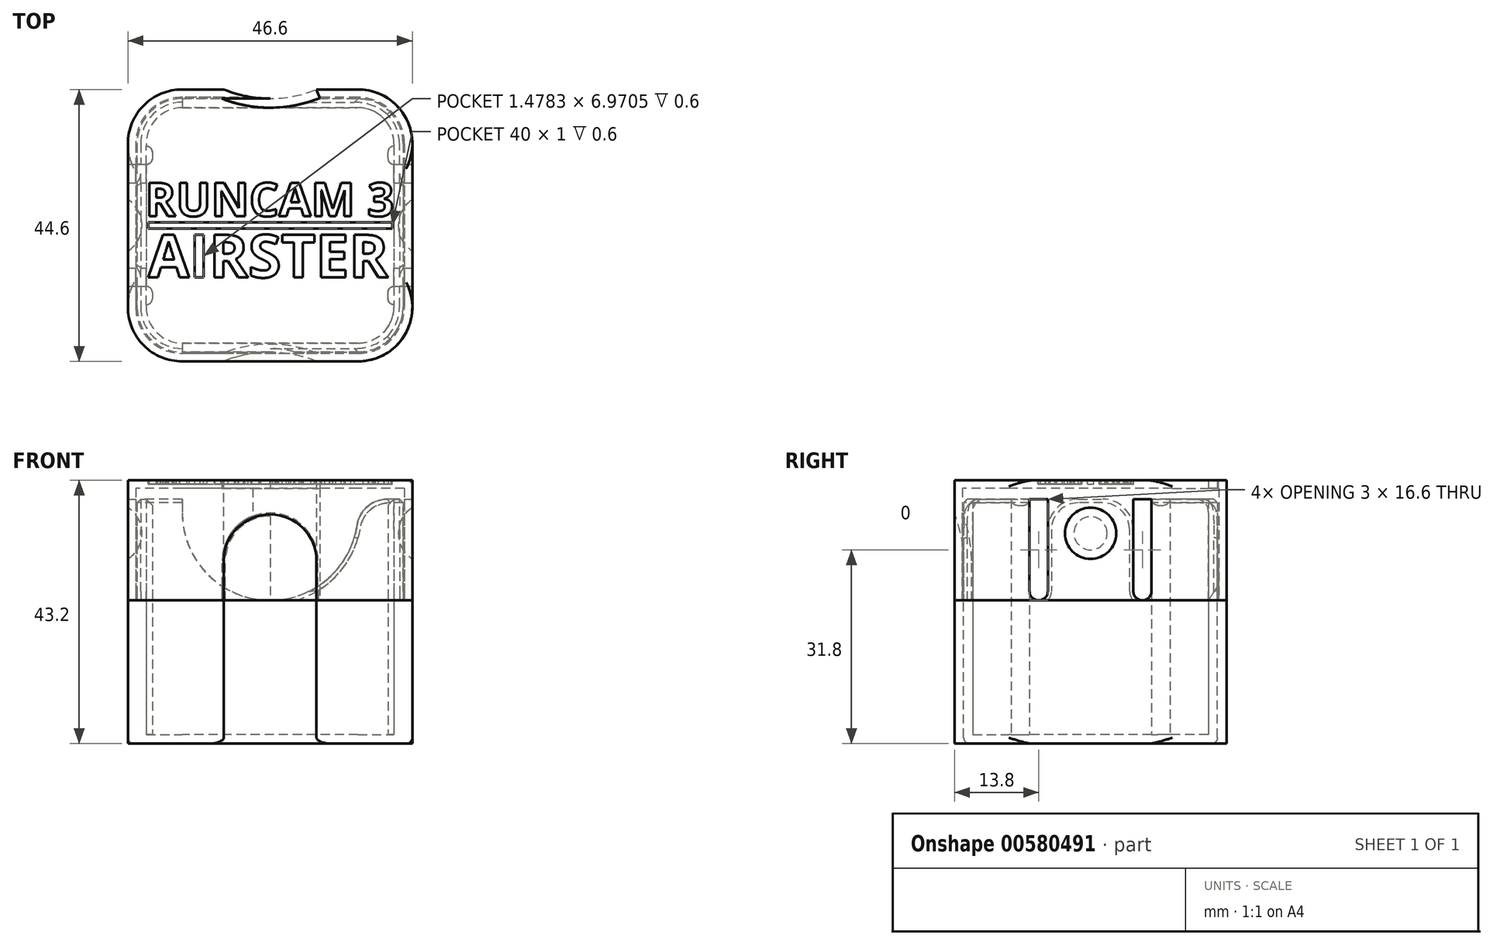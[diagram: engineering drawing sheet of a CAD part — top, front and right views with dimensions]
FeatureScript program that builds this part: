
annotation { "Feature Type Name" : "Feature", "Feature Type Description" : "" }
export const myFeature = defineFeature(function(context is Context, id is Id, definition is map)
    precondition{}
    {
        {
            var Q0;
            Q0=qCreatedBy(makeId("Top.planeOp"),FACE);
            var sketch = newSketch(context, id + "F0", { "sketchPlane" : qUnion([Q0])});
            skLineSegment(sketch, "E0.bottom", {"start": v(14.4, 19.3) * mm, "end": v(-14.4, 19.3) * mm});
            skLineSegment(sketch, "E0.top", {"start": v(14.4, -19.3) * mm, "end": v(-14.4, -19.3) * mm});
            skLineSegment(sketch, "E0.left", {"start": v(20.3, 13.4) * mm, "end": v(20.3, -13.4) * mm});
            skLineSegment(sketch, "E0.right", {"start": v(-20.3, 13.4) * mm, "end": v(-20.3, -13.4) * mm});
            skPoint(sketch, "E0.middle", {"position": v(0, 0) * mm});
            skPoint(sketch, "E1.visualSharp", {"position": v(-20.3, 19.3) * mm});
            skArc(sketch, "E1.filletArc", {"start": v(-14.4, 19.3) * mm, "mid": v(-18.57, 17.57) * mm, "end": v(-20.3, 13.4) * mm});
            skPoint(sketch, "E2.visualSharp", {"position": v(-20.3, -19.3) * mm});
            skArc(sketch, "E2.filletArc", {"start": v(-20.3, -13.4) * mm, "mid": v(-18.57, -17.57) * mm, "end": v(-14.4, -19.3) * mm});
            skPoint(sketch, "E3.visualSharp", {"position": v(20.3, -19.3) * mm});
            skArc(sketch, "E3.filletArc", {"start": v(14.4, -19.3) * mm, "mid": v(18.57, -17.57) * mm, "end": v(20.3, -13.4) * mm});
            skPoint(sketch, "E4.visualSharp", {"position": v(20.3, 19.3) * mm});
            skArc(sketch, "E4.filletArc", {"start": v(20.3, 13.4) * mm, "mid": v(18.57, 17.57) * mm, "end": v(14.4, 19.3) * mm});
            skArc(sketch, "E5.0", {"start": v(21.8, 13.4) * mm, "mid": v(19.63, 18.63) * mm, "end": v(14.4, 20.8) * mm});
            skLineSegment(sketch, "E5.1", {"start": v(14.4, 20.8) * mm, "end": v(-14.4, 20.8) * mm});
            skLineSegment(sketch, "E5.2", {"start": v(21.8, 13.4) * mm, "end": v(21.8, -13.4) * mm});
            skArc(sketch, "E5.3", {"start": v(-14.4, 20.8) * mm, "mid": v(-19.63, 18.63) * mm, "end": v(-21.8, 13.4) * mm});
            skArc(sketch, "E5.4", {"start": v(14.4, -20.8) * mm, "mid": v(19.63, -18.63) * mm, "end": v(21.8, -13.4) * mm});
            skLineSegment(sketch, "E5.5", {"start": v(14.4, -20.8) * mm, "end": v(-14.4, -20.8) * mm});
            skArc(sketch, "E5.6", {"start": v(-21.8, -13.4) * mm, "mid": v(-19.63, -18.63) * mm, "end": v(-14.4, -20.8) * mm});
            skLineSegment(sketch, "E5.7", {"start": v(-21.8, 13.4) * mm, "end": v(-21.8, -13.4) * mm});
            skLineSegment(sketch, "E6.0", {"start": v(23.3, 13.4) * mm, "end": v(23.3, -13.4) * mm});
            skArc(sketch, "E6.1", {"start": v(14.4, -22.3) * mm, "mid": v(20.7, -19.7) * mm, "end": v(23.3, -13.4) * mm});
            skArc(sketch, "E6.2", {"start": v(23.3, 13.4) * mm, "mid": v(20.7, 19.7) * mm, "end": v(14.4, 22.3) * mm});
            skLineSegment(sketch, "E6.3", {"start": v(14.4, -22.3) * mm, "end": v(-14.4, -22.3) * mm});
            skLineSegment(sketch, "E6.4", {"start": v(14.4, 22.3) * mm, "end": v(-14.4, 22.3) * mm});
            skArc(sketch, "E6.5", {"start": v(-14.4, 22.3) * mm, "mid": v(-20.7, 19.7) * mm, "end": v(-23.3, 13.4) * mm});
            skLineSegment(sketch, "E6.6", {"start": v(-23.3, 13.4) * mm, "end": v(-23.3, -13.4) * mm});
            skArc(sketch, "E6.7", {"start": v(-23.3, -13.4) * mm, "mid": v(-20.7, -19.7) * mm, "end": v(-14.4, -22.3) * mm});
            skLineSegment(sketch, "E7.bottom", {"start": v(-20.3, -13) * mm, "end": v(-19.3, -13) * mm});
            skLineSegment(sketch, "E7.top", {"start": v(-20.3, -10) * mm, "end": v(-19.3, -10) * mm});
            skLineSegment(sketch, "E7.left", {"start": v(-20.3, -13) * mm, "end": v(-20.3, -10) * mm});
            skLineSegment(sketch, "E7.right", {"start": v(-19.3, -13) * mm, "end": v(-19.3, -10) * mm});
            skLineSegment(sketch, "E8.MirrorCS", {"start": v(-19.3, 13) * mm, "end": v(-19.3, 10) * mm});
            skLineSegment(sketch, "E9.MirrorCS", {"start": v(-20.3, 10) * mm, "end": v(-19.3, 10) * mm});
            skLineSegment(sketch, "E10.MirrorCS", {"start": v(-20.3, 13) * mm, "end": v(-19.3, 13) * mm});
            skLineSegment(sketch, "E11.MirrorCS", {"start": v(20.3, 13) * mm, "end": v(19.3, 13) * mm});
            skLineSegment(sketch, "E12.MirrorCS", {"start": v(19.3, 13) * mm, "end": v(19.3, 10) * mm});
            skLineSegment(sketch, "E13.MirrorCS", {"start": v(20.3, 10) * mm, "end": v(19.3, 10) * mm});
            skLineSegment(sketch, "E14.MirrorCS", {"start": v(20.3, -10) * mm, "end": v(19.3, -10) * mm});
            skLineSegment(sketch, "E15.MirrorCS", {"start": v(19.3, -13) * mm, "end": v(19.3, -10) * mm});
            skLineSegment(sketch, "E16.MirrorCS", {"start": v(20.3, -13) * mm, "end": v(19.3, -13) * mm});
            skSolve(sketch);
        }
        {
            var Q0;
            Q0=makeQuery(id+"F0.imprint","IMPRINT",FACE,{"disambiguationData":[TD([[makeQuery(id+"F0.imprint","IMPRINT",EDGE,{"derivedFrom":sQuery(id+"F0.wireOp",EDGE,"E0.bottom")}),-1.0]])]});
            var Q1;
            Q1=makeQuery(id+"F0.imprint","IMPRINT",FACE,{"disambiguationData":[TD([[makeQuery(id+"F0.imprint","IMPRINT",EDGE,{"derivedFrom":sQuery(id+"F0.wireOp",EDGE,"E0.bottom")}),1.0]])]});
            var Q2;
            Q2=makeQuery(id+"F0.imprint","IMPRINT",FACE,{"disambiguationData":[TD([[makeQuery(id+"F0.imprint","IMPRINT",EDGE,{"derivedFrom":sQuery(id+"F0.wireOp",EDGE,"E5.0")}),-1.0]])]});
            var Q3;
            Q3=makeQuery(id+"F0.imprint","IMPRINT",FACE,{"disambiguationData":[TD([[makeQuery(id+"F0.imprint","IMPRINT",EDGE,{"derivedFrom":sQuery(id+"F0.wireOp",EDGE,"E5.0")}),1.0]])]});
            var Q4;
            Q4=makeQuery(id+"F0.imprint","IMPRINT",FACE,{"disambiguationData":[TD([[makeQuery(id+"F0.imprint","IMPRINT",EDGE,{"derivedFrom":sQuery(id+"F0.wireOp",EDGE,"E8.MirrorCS")}),-1.0]])]});
            var Q5;
            {var subQ0=sQuery(id+"F0.wireOp",EDGE,"E11.MirrorCS");Q5=makeQuery(id+"F0.imprint","IMPRINT",FACE,{"disambiguationData":[TD([[makeQuery(id+"F0.imprint","IMPRINT",EDGE,{"derivedFrom":subQ0}),1.0]])]});}
            var Q6;
            {var subQ0=sQuery(id+"F0.wireOp",EDGE,"E14.MirrorCS");Q6=makeQuery(id+"F0.imprint","IMPRINT",FACE,{"disambiguationData":[TD([[makeQuery(id+"F0.imprint","IMPRINT",EDGE,{"derivedFrom":subQ0}),1.0]])]});}
            var Q7;
            Q7=makeQuery(id+"F0.imprint","IMPRINT",FACE,{"disambiguationData":[TD([[makeQuery(id+"F0.imprint","IMPRINT",EDGE,{"derivedFrom":sQuery(id+"F0.wireOp",EDGE,"E7.bottom")}),1.0]])]});
            extrude(context, id + "F1", {"entities" : qUnion([Q0, Q1, Q2, Q3, Q4, Q5, Q6, Q7]), "oppositeDirection" : true, "depth" : 1.5 * mm, "offsetDistance" : 25 * mm});
        }
        {
            var Q0;
            Q0=makeQuery(id+"F0.imprint","IMPRINT",FACE,{"disambiguationData":[TD([[makeQuery(id+"F0.imprint","IMPRINT",EDGE,{"derivedFrom":sQuery(id+"F0.wireOp",EDGE,"E0.bottom")}),-1.0]])]});
            var Q1;
            Q1=makeQuery(id+"F0.imprint","IMPRINT",FACE,{"disambiguationData":[TD([[makeQuery(id+"F0.imprint","IMPRINT",EDGE,{"derivedFrom":sQuery(id+"F0.wireOp",EDGE,"E8.MirrorCS")}),-1.0]])]});
            var Q2;
            Q2=makeQuery(id+"F0.imprint","IMPRINT",FACE,{"disambiguationData":[TD([[makeQuery(id+"F0.imprint","IMPRINT",EDGE,{"derivedFrom":sQuery(id+"F0.wireOp",EDGE,"E7.bottom")}),1.0]])]});
            var Q3;
            {var subQ0=sQuery(id+"F0.wireOp",EDGE,"E11.MirrorCS");Q3=makeQuery(id+"F0.imprint","IMPRINT",FACE,{"disambiguationData":[TD([[makeQuery(id+"F0.imprint","IMPRINT",EDGE,{"derivedFrom":subQ0}),1.0]])]});}
            var Q4;
            {var subQ0=sQuery(id+"F0.wireOp",EDGE,"E14.MirrorCS");Q4=makeQuery(id+"F0.imprint","IMPRINT",FACE,{"disambiguationData":[TD([[makeQuery(id+"F0.imprint","IMPRINT",EDGE,{"derivedFrom":subQ0}),1.0]])]});}
            extrude(context, id + "F2", {"entities" : qUnion([Q0, Q1, Q2, Q3, Q4]), "operationType" : NewBodyOperationType.ADD, "depth" : 38.6 * mm, "offsetDistance" : 25 * mm});
        }
        {
            var Q0;
            Q0=makeQuery(id+"F0.imprint","IMPRINT",FACE,{"disambiguationData":[TD([[makeQuery(id+"F0.imprint","IMPRINT",EDGE,{"derivedFrom":sQuery(id+"F0.wireOp",EDGE,"E5.0")}),-1.0]])]});
            var Q1;
            Q1=makeQuery(id+"F0.imprint","IMPRINT",FACE,{"disambiguationData":[TD([[makeQuery(id+"F0.imprint","IMPRINT",EDGE,{"derivedFrom":sQuery(id+"F0.wireOp",EDGE,"E5.0")}),1.0]])]});
            extrude(context, id + "F3", {"entities" : qUnion([Q0, Q1]), "operationType" : NewBodyOperationType.ADD, "depth" : 22 * mm, "offsetDistance" : 25 * mm});
        }
        {
            var Q0;
            Q0=makeQuery(id+"F3.opExtrude","CAP_FACE",FACE,{"disambiguationData":[OSD([sQuery(id+"F0.wireOp",EDGE,"E0.bottom"),sQuery(id+"F0.wireOp",EDGE,"E0.top"),sQuery(id+"F0.wireOp",EDGE,"E0.left"),sQuery(id+"F0.wireOp",EDGE,"E0.right"),sQuery(id+"F0.wireOp",EDGE,"E1.filletArc"),sQuery(id+"F0.wireOp",EDGE,"E2.filletArc"),sQuery(id+"F0.wireOp",EDGE,"E3.filletArc"),sQuery(id+"F0.wireOp",EDGE,"E4.filletArc"),sQuery(id+"F0.wireOp",EDGE,"E6.0"),sQuery(id+"F0.wireOp",EDGE,"E6.1"),sQuery(id+"F0.wireOp",EDGE,"E6.2"),sQuery(id+"F0.wireOp",EDGE,"E6.3"),sQuery(id+"F0.wireOp",EDGE,"E6.4"),sQuery(id+"F0.wireOp",EDGE,"E6.5"),sQuery(id+"F0.wireOp",EDGE,"E6.6"),sQuery(id+"F0.wireOp",EDGE,"E6.7")])],"isStart":false});
            var sketch = newSketch(context, id + "F4", { "sketchPlane" : qUnion([Q0])});
            skSolve(sketch);
        }
        {
            var Q0;
            Q0=makeQuery(id+"F2.opExtrude","SWEPT_FACE",FACE,{"disambiguationData":[OSD([sQuery(id+"F0.wireOp",EDGE,"E5.5")])]});
            var sketch = newSketch(context, id + "F5", { "sketchPlane" : qUnion([Q0])});
            skArc(sketch, "E17", {"start": v(-14.4, 36.4) * mm, "mid": v(0, 22) * mm, "end": v(14.4, 36.4) * mm});
            skSolve(sketch);
        }
        {
            var Q0;
            {var subQ0=sQuery(id+"F0.wireOp",EDGE,"E5.5");var subQ2=makeQuery(id+"F2.opExtrude","CAP_EDGE",EDGE,{"disambiguationData":[OSD([subQ0])],"isStart":false});Q0=makeQuery(id+"F5.imprint","IMPRINT",FACE,{"disambiguationData":[TD([[makeQuery(id+"F5.imprint","IMPRINT",EDGE,{"derivedFrom":subQ2}),1.0]])]});}
            extrude(context, id + "F6", {"entities" : qUnion([Q0]), "operationType" : NewBodyOperationType.REMOVE, "endBound" : BoundingType.THROUGH_ALL, "oppositeDirection" : true, "depth" : 25 * mm, "offsetDistance" : 25 * mm});
        }
        {
            var Q0;
            {var subQ0=sQuery(id+"F0.wireOp",EDGE,"E5.6");var subQ1=sQuery(id+"F0.wireOp",EDGE,"E5.5");var subQ2=sQuery(id+"F0.wireOp",EDGE,"E2.filletArc");Q0=makeQuery(id+"F6.boolean.opBoolean","COPY",EDGE,{"disambiguationData":[TD([makeQuery(id+"F2.opExtrude","SWEPT_FACE",FACE,{"disambiguationData":[OSD([subQ2])]})])],"derivedFrom":makeQuery(id+"F6.opExtrude","SWEPT_EDGE",EDGE,{"disambiguationData":[OSD([subQ1,subQ0])]})});}
            var Q1;
            {var subQ0=sQuery(id+"F0.wireOp",EDGE,"E5.5");var subQ1=sQuery(id+"F0.wireOp",EDGE,"E5.4");var subQ2=sQuery(id+"F0.wireOp",EDGE,"E3.filletArc");Q1=makeQuery(id+"F6.boolean.opBoolean","COPY",EDGE,{"disambiguationData":[TD([makeQuery(id+"F2.opExtrude","SWEPT_FACE",FACE,{"disambiguationData":[OSD([subQ2])]})])],"derivedFrom":makeQuery(id+"F6.opExtrude","SWEPT_EDGE",EDGE,{"disambiguationData":[OSD([subQ1,subQ0])]})});}
            var Q2;
            {var subQ0=sQuery(id+"F0.wireOp",EDGE,"E5.5");var subQ1=sQuery(id+"F0.wireOp",EDGE,"E5.4");var subQ3=sQuery(id+"F0.wireOp",EDGE,"E4.filletArc");Q2=makeQuery(id+"F6.boolean.opBoolean","COPY",EDGE,{"disambiguationData":[TD([makeQuery(id+"F2.opExtrude","SWEPT_FACE",FACE,{"disambiguationData":[OSD([subQ3])]})])],"derivedFrom":makeQuery(id+"F6.opExtrude","SWEPT_EDGE",EDGE,{"disambiguationData":[OSD([subQ1,subQ0])]})});}
            var Q3;
            {var subQ0=sQuery(id+"F0.wireOp",EDGE,"E5.6");var subQ1=sQuery(id+"F0.wireOp",EDGE,"E5.5");var subQ3=sQuery(id+"F0.wireOp",EDGE,"E1.filletArc");Q3=makeQuery(id+"F6.boolean.opBoolean","COPY",EDGE,{"disambiguationData":[TD([makeQuery(id+"F2.opExtrude","SWEPT_FACE",FACE,{"disambiguationData":[OSD([subQ3])]})])],"derivedFrom":makeQuery(id+"F6.opExtrude","SWEPT_EDGE",EDGE,{"disambiguationData":[OSD([subQ1,subQ0])]})});}
            fillet(context, id + "F7", {"entities" : qUnion([Q0, Q1, Q2, Q3]), "radius" : 5 * mm, "tangentPropagation" : true, "allowEdgeOverflow" : false});
        }
        {
            var Q0;
            Q0=makeQuery(id+"F2.opExtrude","SWEPT_EDGE",EDGE,{"disambiguationData":[OSD([sQuery(id+"F0.wireOp",EDGE,"E8.MirrorCS"),sQuery(id+"F0.wireOp",EDGE,"E9.MirrorCS")])]});
            var Q1;
            Q1=makeQuery(id+"F2.opExtrude","SWEPT_EDGE",EDGE,{"disambiguationData":[OSD([sQuery(id+"F0.wireOp",EDGE,"E8.MirrorCS"),sQuery(id+"F0.wireOp",EDGE,"E10.MirrorCS")])]});
            var Q2;
            Q2=makeQuery(id+"F2.opExtrude","SWEPT_EDGE",EDGE,{"disambiguationData":[OSD([sQuery(id+"F0.wireOp",EDGE,"E7.bottom"),sQuery(id+"F0.wireOp",EDGE,"E7.right")])]});
            var Q3;
            Q3=makeQuery(id+"F2.opExtrude","SWEPT_EDGE",EDGE,{"disambiguationData":[OSD([sQuery(id+"F0.wireOp",EDGE,"E7.top"),sQuery(id+"F0.wireOp",EDGE,"E7.right")])]});
            var Q4;
            Q4=makeQuery(id+"F2.opExtrude","SWEPT_EDGE",EDGE,{"disambiguationData":[OSD([sQuery(id+"F0.wireOp",EDGE,"E12.MirrorCS"),sQuery(id+"F0.wireOp",EDGE,"E13.MirrorCS")])]});
            var Q5;
            Q5=makeQuery(id+"F2.opExtrude","SWEPT_EDGE",EDGE,{"disambiguationData":[OSD([sQuery(id+"F0.wireOp",EDGE,"E14.MirrorCS"),sQuery(id+"F0.wireOp",EDGE,"E15.MirrorCS")])]});
            var Q6;
            Q6=makeQuery(id+"F2.opExtrude","SWEPT_EDGE",EDGE,{"disambiguationData":[OSD([sQuery(id+"F0.wireOp",EDGE,"E15.MirrorCS"),sQuery(id+"F0.wireOp",EDGE,"E16.MirrorCS")])]});
            var Q7;
            Q7=makeQuery(id+"F2.opExtrude","SWEPT_EDGE",EDGE,{"disambiguationData":[OSD([sQuery(id+"F0.wireOp",EDGE,"E11.MirrorCS"),sQuery(id+"F0.wireOp",EDGE,"E12.MirrorCS")])]});
            fillet(context, id + "F8", {"entities" : qUnion([Q0, Q1, Q2, Q3, Q4, Q5, Q6, Q7]), "radius" : 1 * mm, "tangentPropagation" : true, "allowEdgeOverflow" : false});
        }
        {
            var Q0;
            {var subQ7=sQuery(id+"F0.wireOp",EDGE,"E6.0");Q0=makeQuery(id+"F4.imprint","IMPRINT",FACE,{"disambiguationData":[TD([[makeQuery(id+"F4.imprint","IMPRINT",EDGE,{"derivedFrom":makeQuery(id+"F3.opExtrude","CAP_EDGE",EDGE,{"disambiguationData":[OSD([subQ7])],"isStart":false})}),-1.0]])]});}
            var Q1;
            {var subQ0=makeQuery(id+"F3.opExtrude","CAP_FACE",FACE,{"disambiguationData":[OSD([sQuery(id+"F0.wireOp",EDGE,"E0.bottom"),sQuery(id+"F0.wireOp",EDGE,"E0.top"),sQuery(id+"F0.wireOp",EDGE,"E0.left"),sQuery(id+"F0.wireOp",EDGE,"E0.right"),sQuery(id+"F0.wireOp",EDGE,"E1.filletArc"),sQuery(id+"F0.wireOp",EDGE,"E2.filletArc"),sQuery(id+"F0.wireOp",EDGE,"E3.filletArc"),sQuery(id+"F0.wireOp",EDGE,"E4.filletArc"),sQuery(id+"F0.wireOp",EDGE,"E6.0"),sQuery(id+"F0.wireOp",EDGE,"E6.1"),sQuery(id+"F0.wireOp",EDGE,"E6.2"),sQuery(id+"F0.wireOp",EDGE,"E6.3"),sQuery(id+"F0.wireOp",EDGE,"E6.4"),sQuery(id+"F0.wireOp",EDGE,"E6.5"),sQuery(id+"F0.wireOp",EDGE,"E6.6"),sQuery(id+"F0.wireOp",EDGE,"E6.7")])],"isStart":false});Q1=makeQuery(id+"F4.imprint","IMPRINT",FACE,{"disambiguationData":[TD([[makeQuery(id+"F4.imprint","IMPRINT",EDGE,{"derivedFrom":makeQuery(id+"F3.boolean.opBoolean","INTERSECT",EDGE,{"derivedFrom":[makeQuery(id+"F2.opExtrude","SWEPT_FACE",FACE,{"disambiguationData":[OSD([sQuery(id+"F0.wireOp",EDGE,"E5.0")])]}),subQ0]})}),1.0]])]});}
            var Q2;
            {var subQ0=sQuery(id+"F0.wireOp",EDGE,"760bae26-e821-4f93-9cbd-1cc9cc26cd04.2");var subQ1=sQuery(id+"F0.wireOp",EDGE,"E2.filletArc");var subQ2=sQuery(id+"F0.wireOp",EDGE,"E1.filletArc");var subQ3=sQuery(id+"F0.wireOp",EDGE,"E0.right");var subQ4=sQuery(id+"F0.wireOp",EDGE,"760bae26-e821-4f93-9cbd-1cc9cc26cd04.4");var subQ5=sQuery(id+"F0.wireOp",EDGE,"760bae26-e821-4f93-9cbd-1cc9cc26cd04.6");var subQ6=sQuery(id+"F0.wireOp",EDGE,"760bae26-e821-4f93-9cbd-1cc9cc26cd04.5");Q2=makeQuery(id+"F6.boolean.opBoolean","SPLIT",FACE,{"disambiguationData":[TD([makeQuery(id+"F2.opExtrude","SWEPT_FACE",FACE,{"disambiguationData":[OSD([subQ3])]})])],"derivedFrom":makeQuery(id+"F2.opExtrude","CAP_FACE",FACE,{"disambiguationData":[OSD([sQuery(id+"F0.wireOp",EDGE,"E0.bottom"),sQuery(id+"F0.wireOp",EDGE,"E0.top"),sQuery(id+"F0.wireOp",EDGE,"E0.left"),subQ3,subQ2,subQ1,sQuery(id+"F0.wireOp",EDGE,"E3.filletArc"),sQuery(id+"F0.wireOp",EDGE,"E4.filletArc"),sQuery(id+"F0.wireOp",EDGE,"760bae26-e821-4f93-9cbd-1cc9cc26cd04.0"),sQuery(id+"F0.wireOp",EDGE,"760bae26-e821-4f93-9cbd-1cc9cc26cd04.1"),subQ0,sQuery(id+"F0.wireOp",EDGE,"760bae26-e821-4f93-9cbd-1cc9cc26cd04.3"),subQ4,subQ6,subQ5,sQuery(id+"F0.wireOp",EDGE,"760bae26-e821-4f93-9cbd-1cc9cc26cd04.7")])],"isStart":false})});}
            extrude(context, id + "F9", {"entities" : qUnion([Q0, Q1]), "depth" : 19.7 * mm, "endBoundEntityFace" : qUnion([Q2]), "hasOffset" : true, "offsetDistance" : -1.5 * mm});
        }
        {
            var Q0;
            Q0=makeQuery(id+"F9.opExtrude","SWEPT_FACE",FACE,{"disambiguationData":[OSD([sQuery(id+"F0.wireOp",EDGE,"E6.3")])]});
            cPlane(context, id + "F10", {"entities" : qUnion([Q0]), "cplaneType" : CPlaneType.OFFSET, "offset" : 18.5 * mm, "width" : 150 * mm, "height" : 150 * mm});
        }
        {
            var Q0;
            Q0=qCreatedBy(id+"F10.planeOp",FACE);
            var sketch = newSketch(context, id + "F11", { "sketchPlane" : qUnion([Q0])});
            skArc(sketch, "E18", {"start": v(0, 8.5) * mm, "mid": v(20, 28.5) * mm, "end": v(0, 48.5) * mm});
            skLineSegment(sketch, "E19", {"start": v(0, 48.5) * mm, "end": v(0, 8.5) * mm});
            skLineSegment(sketch, "E20", {"start": v(0, 28.5) * mm, "end": v(20, 28.5) * mm});
            skSolve(sketch);
        }
        {
            var Q0;
            {var subQ3=sQuery(id+"F11.wireOp",EDGE,"E20");Q0=makeQuery(id+"F11.imprint","IMPRINT",FACE,{"disambiguationData":[TD([[makeQuery(id+"F11.imprint","IMPRINT",EDGE,{"derivedFrom":subQ3}),1.0]])]});}
            var Q1;
            Q1=sQuery(id+"F11.wireOp",EDGE,"E19");
            revolve(context, id + "F12", {"entities" : qUnion([Q0]), "axis" : qUnion([Q1]), "revolveType" : RevolveType.ONE_DIRECTION, "oppositeDirection" : true, "angle" : 180 * degree});
        }
        {
            var Q0;
            Q0=makeQuery(id+"F12.opRevolve","SWEPT_BODY",BODY,{"disambiguationData":[OSD([sQuery(id+"F11.wireOp",EDGE,"E18"),sQuery(id+"F11.wireOp",EDGE,"E19")])]});
            var Q1;
            Q1=qCreatedBy(makeId("Front.planeOp"),FACE);
            mirror(context, id + "F13", {"entities" : qUnion([Q0]), "mirrorPlane" : qUnion([Q1])});
        }
        {
            var Q0;
            Q0=makeQuery(id+"F13.opPattern","COPY",BODY,{"derivedFrom":makeQuery(id+"F12.opRevolve","SWEPT_BODY",BODY,{"disambiguationData":[OSD([sQuery(id+"F11.wireOp",EDGE,"E18"),sQuery(id+"F11.wireOp",EDGE,"E19")])]}),"instanceName":"1"});
            var Q1;
            Q1=makeQuery(id+"F12.opRevolve","SWEPT_BODY",BODY,{"disambiguationData":[OSD([sQuery(id+"F11.wireOp",EDGE,"E18"),sQuery(id+"F11.wireOp",EDGE,"E19")])]});
            var Q2;
            Q2=makeQuery(id+"F9.opExtrude","SWEPT_BODY",BODY,{"disambiguationData":[OSD([sQuery(id+"F0.wireOp",EDGE,"E6.0"),sQuery(id+"F0.wireOp",EDGE,"E6.1"),sQuery(id+"F0.wireOp",EDGE,"E6.2"),sQuery(id+"F0.wireOp",EDGE,"E6.3"),sQuery(id+"F0.wireOp",EDGE,"E6.4"),sQuery(id+"F0.wireOp",EDGE,"E6.5"),sQuery(id+"F0.wireOp",EDGE,"E6.6"),sQuery(id+"F0.wireOp",EDGE,"E6.7")])]});
            var Q3;
            Q3=makeQuery(id+"F1.opExtrude","SWEPT_BODY",BODY,{"disambiguationData":[OSD([sQuery(id+"F0.wireOp",EDGE,"E6.0"),sQuery(id+"F0.wireOp",EDGE,"E6.1"),sQuery(id+"F0.wireOp",EDGE,"E6.2"),sQuery(id+"F0.wireOp",EDGE,"E6.3"),sQuery(id+"F0.wireOp",EDGE,"E6.4"),sQuery(id+"F0.wireOp",EDGE,"E6.5"),sQuery(id+"F0.wireOp",EDGE,"E6.6"),sQuery(id+"F0.wireOp",EDGE,"E6.7")])]});
            booleanBodies(context, id + "F14", {"operationType" : BooleanOperationType.SUBTRACTION, "tools" : qUnion([Q0, Q1]), "targets" : qUnion([Q2, Q3])});
        }
        {
            var Q0;
            Q0=makeQuery(id+"F14.opBoolean","COPY",FACE,{"derivedFrom":makeQuery(id+"F12.opRevolve","SWEPT_FACE",FACE,{"disambiguationData":[OSD([sQuery(id+"F11.wireOp",EDGE,"E20")])]})});
            var Q1;
            Q1=makeQuery(id+"F14.opBoolean","COPY",FACE,{"derivedFrom":makeQuery(id+"F13.opPattern","COPY",FACE,{"derivedFrom":makeQuery(id+"F12.opRevolve","SWEPT_FACE",FACE,{"disambiguationData":[OSD([sQuery(id+"F11.wireOp",EDGE,"E20")])]}),"instanceName":"1"})});
            extrude(context, id + "F15", {"entities" : qUnion([Q0, Q1]), "operationType" : NewBodyOperationType.REMOVE, "endBound" : BoundingType.THROUGH_ALL, "oppositeDirection" : true, "depth" : 25 * mm, "offsetDistance" : 25 * mm});
        }
        {
            var Q0;
            {var subQ0=sQuery(id+"F11.wireOp",EDGE,"E20");var subQ1=sQuery(id+"F11.wireOp",EDGE,"E18");Q0=makeQuery(id+"F15.boolean.opBoolean","INTERSECT",EDGE,{"derivedFrom":[makeQuery(id+"F1.opExtrude","CAP_FACE",FACE,{"disambiguationData":[OSD([sQuery(id+"F0.wireOp",EDGE,"E6.0"),sQuery(id+"F0.wireOp",EDGE,"E6.1"),sQuery(id+"F0.wireOp",EDGE,"E6.2"),sQuery(id+"F0.wireOp",EDGE,"E6.3"),sQuery(id+"F0.wireOp",EDGE,"E6.4"),sQuery(id+"F0.wireOp",EDGE,"E6.5"),sQuery(id+"F0.wireOp",EDGE,"E6.6"),sQuery(id+"F0.wireOp",EDGE,"E6.7")])],"isStart":false}),makeQuery(id+"F15.opExtrude","SWEPT_FACE",FACE,{"disambiguationData":[OSD([subQ1,subQ0]),TDD([makeQuery(id+"F14.opBoolean","COPY",EDGE,{"derivedFrom":makeQuery(id+"F12.opRevolve","SWEPT_EDGE",EDGE,{"disambiguationData":[OSD([subQ1,subQ0])]})})])]})]});}
            var Q1;
            Q1=makeQuery(id+"F1.opExtrude","CAP_EDGE",EDGE,{"disambiguationData":[OSD([sQuery(id+"F0.wireOp",EDGE,"E6.0")])],"isStart":false});
            var Q2;
            Q2=makeQuery(id+"F1.opExtrude","CAP_EDGE",EDGE,{"disambiguationData":[OSD([sQuery(id+"F0.wireOp",EDGE,"E6.6")])],"isStart":false});
            var Q3;
            {var subQ0=sQuery(id+"F11.wireOp",EDGE,"E20");var subQ1=sQuery(id+"F11.wireOp",EDGE,"E18");Q3=makeQuery(id+"F15.boolean.opBoolean","INTERSECT",EDGE,{"derivedFrom":[makeQuery(id+"F1.opExtrude","CAP_FACE",FACE,{"disambiguationData":[OSD([sQuery(id+"F0.wireOp",EDGE,"E6.0"),sQuery(id+"F0.wireOp",EDGE,"E6.1"),sQuery(id+"F0.wireOp",EDGE,"E6.2"),sQuery(id+"F0.wireOp",EDGE,"E6.3"),sQuery(id+"F0.wireOp",EDGE,"E6.4"),sQuery(id+"F0.wireOp",EDGE,"E6.5"),sQuery(id+"F0.wireOp",EDGE,"E6.6"),sQuery(id+"F0.wireOp",EDGE,"E6.7")])],"isStart":false}),makeQuery(id+"F15.opExtrude","SWEPT_FACE",FACE,{"disambiguationData":[OSD([subQ1,subQ0]),TDD([makeQuery(id+"F14.opBoolean","COPY",EDGE,{"derivedFrom":makeQuery(id+"F13.opPattern","COPY",EDGE,{"derivedFrom":makeQuery(id+"F12.opRevolve","SWEPT_EDGE",EDGE,{"disambiguationData":[OSD([subQ1,subQ0])]}),"instanceName":"1"})})])]})]});}
            fillet(context, id + "F16", {"entities" : qUnion([Q0, Q1, Q2, Q3]), "radius" : 1 * mm, "tangentPropagation" : true, "allowEdgeOverflow" : false});
        }
        {
            var Q0;
            Q0=makeQuery(id+"F9.opExtrude","CAP_FACE",FACE,{"disambiguationData":[OSD([sQuery(id+"F0.wireOp",EDGE,"E6.0"),sQuery(id+"F0.wireOp",EDGE,"E6.1"),sQuery(id+"F0.wireOp",EDGE,"E6.2"),sQuery(id+"F0.wireOp",EDGE,"E6.3"),sQuery(id+"F0.wireOp",EDGE,"E6.4"),sQuery(id+"F0.wireOp",EDGE,"E6.5"),sQuery(id+"F0.wireOp",EDGE,"E6.6"),sQuery(id+"F0.wireOp",EDGE,"E6.7")])],"isStart":true});
            shell(context, id + "F17", {"entities" : qUnion([Q0]), "thickness" : 1.3 * mm});
        }
        {
            var Q0;
            Q0=makeQuery(id+"F9.opExtrude","SWEPT_FACE",FACE,{"disambiguationData":[OSD([sQuery(id+"F0.wireOp",EDGE,"E6.0")])]});
            cPlane(context, id + "F18", {"entities" : qUnion([Q0]), "cplaneType" : CPlaneType.OFFSET, "offset" : 2.7 * mm, "width" : 150 * mm, "height" : 150 * mm});
        }
        {
            var Q0;
            Q0=qCreatedBy(id+"F18.planeOp",FACE);
            var sketch = newSketch(context, id + "F19", { "sketchPlane" : qUnion([Q0])});
            skArc(sketch, "E21", {"start": v(0, 28) * mm, "mid": v(5, 33) * mm, "end": v(0, 38) * mm});
            skLineSegment(sketch, "E22", {"start": v(0, 38) * mm, "end": v(0, 28) * mm});
            skLineSegment(sketch, "E23.bottom", {"start": v(-10, 38.6) * mm, "end": v(-7, 38.6) * mm});
            skLineSegment(sketch, "E23.top", {"start": v(-8.5, 22) * mm, "end": v(-8.5, 22) * mm});
            skLineSegment(sketch, "E23.left", {"start": v(-10, 38.6) * mm, "end": v(-10, 23.5) * mm});
            skLineSegment(sketch, "E23.right", {"start": v(-7, 38.6) * mm, "end": v(-7, 23.5) * mm});
            skLineSegment(sketch, "E24.MirrorCS", {"start": v(7, 38.6) * mm, "end": v(7, 23.5) * mm});
            skLineSegment(sketch, "E25.MirrorCS", {"start": v(10, 38.6) * mm, "end": v(10, 23.5) * mm});
            skLineSegment(sketch, "E26.MirrorCS", {"start": v(10, 38.6) * mm, "end": v(7, 38.6) * mm});
            skLineSegment(sketch, "E27.MirrorCS", {"start": v(8.5, 22) * mm, "end": v(8.5, 22) * mm});
            skPoint(sketch, "E28.visualSharp", {"position": v(-10, 22) * mm});
            skArc(sketch, "E28.filletArc", {"start": v(-10, 23.5) * mm, "mid": v(-9.56, 22.44) * mm, "end": v(-8.5, 22) * mm});
            skPoint(sketch, "E29.visualSharp", {"position": v(-7, 22) * mm});
            skArc(sketch, "E29.filletArc", {"start": v(-8.5, 22) * mm, "mid": v(-7.44, 22.44) * mm, "end": v(-7, 23.5) * mm});
            skPoint(sketch, "E30.visualSharp", {"position": v(7, 22) * mm});
            skArc(sketch, "E30.filletArc", {"start": v(7, 23.5) * mm, "mid": v(7.44, 22.44) * mm, "end": v(8.5, 22) * mm});
            skPoint(sketch, "E31.visualSharp", {"position": v(10, 22) * mm});
            skArc(sketch, "E31.filletArc", {"start": v(8.5, 22) * mm, "mid": v(9.56, 22.44) * mm, "end": v(10, 23.5) * mm});
            skSolve(sketch);
        }
        {
            var Q0;
            Q0=makeQuery(id+"F19.imprint","IMPRINT",FACE,{"disambiguationData":[TD([[makeQuery(id+"F19.imprint","IMPRINT",EDGE,{"derivedFrom":sQuery(id+"F19.wireOp",EDGE,"E21")}),1.0]])]});
            var Q1;
            Q1=sQuery(id+"F19.wireOp",EDGE,"E22");
            revolve(context, id + "F20", {"entities" : qUnion([Q0]), "axis" : qUnion([Q1]), "revolveType" : RevolveType.ONE_DIRECTION, "oppositeDirection" : true, "angle" : 180 * degree});
        }
        {
            var Q0;
            Q0=makeQuery(id+"F20.opRevolve","SWEPT_BODY",BODY,{"disambiguationData":[OSD([sQuery(id+"F19.wireOp",EDGE,"E21"),sQuery(id+"F19.wireOp",EDGE,"E22")])]});
            var Q1;
            Q1=qCreatedBy(makeId("Right.planeOp"),FACE);
            mirror(context, id + "F21", {"entities" : qUnion([Q0]), "mirrorPlane" : qUnion([Q1])});
        }
        {
            var Q0;
            Q0=makeQuery(id+"F21.opPattern","COPY",BODY,{"derivedFrom":makeQuery(id+"F20.opRevolve","SWEPT_BODY",BODY,{"disambiguationData":[OSD([sQuery(id+"F19.wireOp",EDGE,"E21"),sQuery(id+"F19.wireOp",EDGE,"E22")])]}),"instanceName":"1"});
            var Q1;
            Q1=makeQuery(id+"F20.opRevolve","SWEPT_BODY",BODY,{"disambiguationData":[OSD([sQuery(id+"F19.wireOp",EDGE,"E21"),sQuery(id+"F19.wireOp",EDGE,"E22")])]});
            var Q2;
            Q2=makeQuery(id+"F1.opExtrude","SWEPT_BODY",BODY,{"disambiguationData":[OSD([sQuery(id+"F0.wireOp",EDGE,"E6.0"),sQuery(id+"F0.wireOp",EDGE,"E6.1"),sQuery(id+"F0.wireOp",EDGE,"E6.2"),sQuery(id+"F0.wireOp",EDGE,"E6.3"),sQuery(id+"F0.wireOp",EDGE,"E6.4"),sQuery(id+"F0.wireOp",EDGE,"E6.5"),sQuery(id+"F0.wireOp",EDGE,"E6.6"),sQuery(id+"F0.wireOp",EDGE,"E6.7")])]});
            booleanBodies(context, id + "F22", {"operationType" : BooleanOperationType.SUBTRACTION, "tools" : qUnion([Q0, Q1]), "targets" : qUnion([Q2]), "keepTools" : true});
        }
        {
            var Q0;
            Q0=makeQuery(id+"F21.opPattern","COPY",FACE,{"derivedFrom":makeQuery(id+"F20.opRevolve","CAP_FACE",FACE,{"disambiguationData":[OSD([sQuery(id+"F19.wireOp",EDGE,"E21"),sQuery(id+"F19.wireOp",EDGE,"E22")])],"isStart":true}),"instanceName":"1"});
            var Q1;
            Q1=makeQuery(id+"F9.opExtrude","SWEPT_FACE",FACE,{"disambiguationData":[OSD([sQuery(id+"F0.wireOp",EDGE,"E6.6")])]});
            extrude(context, id + "F23", {"entities" : qUnion([Q0]), "operationType" : NewBodyOperationType.REMOVE, "endBound" : BoundingType.UP_TO_SURFACE, "oppositeDirection" : true, "depth" : 25 * mm, "endBoundEntityFace" : qUnion([Q1]), "offsetDistance" : 25 * mm});
        }
        {
            var Q0;
            Q0=makeQuery(id+"F20.opRevolve","CAP_FACE",FACE,{"disambiguationData":[OSD([sQuery(id+"F19.wireOp",EDGE,"E21"),sQuery(id+"F19.wireOp",EDGE,"E22")])],"isStart":true});
            var Q1;
            Q1=makeQuery(id+"F9.opExtrude","SWEPT_FACE",FACE,{"disambiguationData":[OSD([sQuery(id+"F0.wireOp",EDGE,"E6.0")])]});
            extrude(context, id + "F24", {"entities" : qUnion([Q0]), "operationType" : NewBodyOperationType.REMOVE, "endBound" : BoundingType.UP_TO_SURFACE, "oppositeDirection" : true, "depth" : 25 * mm, "endBoundEntityFace" : qUnion([Q1]), "offsetDistance" : 25 * mm});
        }
        {
            var Q0;
            {var subQ0=sQuery(id+"F4.wireOp",EDGE,"85f63282-6bf9-4db7-9a1d-20234ae27612.7");var subQ1=sQuery(id+"F4.wireOp",EDGE,"85f63282-6bf9-4db7-9a1d-20234ae27612.6");var subQ2=sQuery(id+"F4.wireOp",EDGE,"85f63282-6bf9-4db7-9a1d-20234ae27612.5");var subQ3=sQuery(id+"F4.wireOp",EDGE,"85f63282-6bf9-4db7-9a1d-20234ae27612.4");var subQ4=sQuery(id+"F4.wireOp",EDGE,"85f63282-6bf9-4db7-9a1d-20234ae27612.3");var subQ5=sQuery(id+"F4.wireOp",EDGE,"85f63282-6bf9-4db7-9a1d-20234ae27612.2");var subQ6=sQuery(id+"F4.wireOp",EDGE,"85f63282-6bf9-4db7-9a1d-20234ae27612.1");var subQ7=sQuery(id+"F4.wireOp",EDGE,"85f63282-6bf9-4db7-9a1d-20234ae27612.0");Q0=makeQuery(id+"FcbCElI8lbq80RP_2.boolean.opBoolean","MERGE",FACE,{"derivedFrom":[makeQuery(id+"F9.opExtrude","CAP_FACE",FACE,{"disambiguationData":[OSD([sQuery(id+"F0.wireOp",EDGE,"E6.0"),sQuery(id+"F0.wireOp",EDGE,"E6.1"),sQuery(id+"F0.wireOp",EDGE,"E6.2"),sQuery(id+"F0.wireOp",EDGE,"E6.3"),sQuery(id+"F0.wireOp",EDGE,"E6.4"),sQuery(id+"F0.wireOp",EDGE,"E6.5"),sQuery(id+"F0.wireOp",EDGE,"E6.6"),sQuery(id+"F0.wireOp",EDGE,"E6.7"),subQ7,subQ6,subQ5,subQ4,subQ3,subQ2,subQ1,subQ0])],"isStart":false}),makeQuery(id+"FcbCElI8lbq80RP_2.opExtrude","CAP_FACE",FACE,{"disambiguationData":[OSD([subQ7,subQ6,subQ5,subQ4,subQ3,subQ2,subQ1,subQ0])],"isStart":true})]});}
            var sketch = newSketch(context, id + "F25", { "sketchPlane" : qUnion([Q0])});
            skText(sketch, "E32", { "text": "AIRSTER", "fontName": "OpenSans-Bold.ttf"});
            skText(sketch, "E33", { "text": "RUNCAM 3", "fontName": "OpenSans-Bold.ttf"});
            skLineSegment(sketch, "E34.bottom", {"start": v(-20, -0.5) * mm, "end": v(20, -0.5) * mm});
            skLineSegment(sketch, "E34.top", {"start": v(-20, 0.5) * mm, "end": v(20, 0.5) * mm});
            skLineSegment(sketch, "E34.left", {"start": v(-20, -0.5) * mm, "end": v(-20, 0.5) * mm});
            skLineSegment(sketch, "E34.right", {"start": v(20, -0.5) * mm, "end": v(20, 0.5) * mm});
            skPoint(sketch, "E34.middle", {"position": v(0, 0) * mm});
            const initialGuessF25  = {"E32": [-0.02, -0.00853, 1, 0, 0.00703], "E33": [-0.0205, 0.0015, 1, 0, 0.00551]};
            skSetInitialGuess(sketch, initialGuessF25);
            skSolve(sketch);
        }
        {
            var Q0;
            Q0 = qSketchRegion(id + "F25", true);
            extrude(context, id + "F26", {"entities" : qUnion([Q0]), "operationType" : NewBodyOperationType.REMOVE, "oppositeDirection" : true, "depth" : 0.6 * mm, "offsetDistance" : 25 * mm});
        }
        {
            var Q0;
            Q0=makeQuery(id+"F9.opExtrude","CAP_EDGE",EDGE,{"disambiguationData":[OSD([sQuery(id+"F0.wireOp",EDGE,"E6.0")])],"isStart":false});
            fillet(context, id + "F27", {"entities" : qUnion([Q0]), "radius" : 1 * mm, "tangentPropagation" : true, "allowEdgeOverflow" : false});
        }
        {
            var Q0;
            Q0=makeQuery(id+"F19.imprint","IMPRINT",FACE,{"disambiguationData":[TD([[makeQuery(id+"F19.imprint","IMPRINT",EDGE,{"derivedFrom":sQuery(id+"F19.wireOp",EDGE,"E23.bottom")}),-1.0]])]});
            var Q1;
            Q1=makeQuery(id+"F19.imprint","IMPRINT",FACE,{"disambiguationData":[TD([[makeQuery(id+"F19.imprint","IMPRINT",EDGE,{"derivedFrom":sQuery(id+"F19.wireOp",EDGE,"E24.MirrorCS")}),1.0]])]});
            extrude(context, id + "F28", {"entities" : qUnion([Q0, Q1]), "operationType" : NewBodyOperationType.REMOVE, "endBound" : BoundingType.THROUGH_ALL, "oppositeDirection" : true, "depth" : 25 * mm, "offsetDistance" : 25 * mm});
        }
        {
            var Q0;
            {var subQ1=sQuery(id+"F0.wireOp",EDGE,"E0.left");var subQ2=sQuery(id+"F19.wireOp",EDGE,"E23.left");Q0=makeQuery(id+"F28.boolean.opBoolean","COPY",EDGE,{"disambiguationData":[TD([makeQuery(id+"F2.opExtrude","SWEPT_FACE",FACE,{"disambiguationData":[OSD([subQ1])]})])],"derivedFrom":makeQuery(id+"F28.opExtrude","SWEPT_EDGE",EDGE,{"disambiguationData":[OSD([sQuery(id+"F19.wireOp",EDGE,"E23.bottom"),subQ2])]})});}
            var Q1;
            {var subQ1=sQuery(id+"F0.wireOp",EDGE,"E0.left");var subQ2=sQuery(id+"F19.wireOp",EDGE,"E23.right");Q1=makeQuery(id+"F28.boolean.opBoolean","COPY",EDGE,{"disambiguationData":[TD([makeQuery(id+"F2.opExtrude","SWEPT_FACE",FACE,{"disambiguationData":[OSD([subQ1])]})])],"derivedFrom":makeQuery(id+"F28.opExtrude","SWEPT_EDGE",EDGE,{"disambiguationData":[OSD([sQuery(id+"F19.wireOp",EDGE,"E23.bottom"),subQ2])]})});}
            var Q2;
            {var subQ1=sQuery(id+"F0.wireOp",EDGE,"E0.left");var subQ2=sQuery(id+"F19.wireOp",EDGE,"E24.MirrorCS");Q2=makeQuery(id+"F28.boolean.opBoolean","COPY",EDGE,{"disambiguationData":[TD([makeQuery(id+"F2.opExtrude","SWEPT_FACE",FACE,{"disambiguationData":[OSD([subQ1])]})])],"derivedFrom":makeQuery(id+"F28.opExtrude","SWEPT_EDGE",EDGE,{"disambiguationData":[OSD([subQ2,sQuery(id+"F19.wireOp",EDGE,"E26.MirrorCS")])]})});}
            var Q3;
            {var subQ1=sQuery(id+"F0.wireOp",EDGE,"E0.left");var subQ2=sQuery(id+"F19.wireOp",EDGE,"E25.MirrorCS");Q3=makeQuery(id+"F28.boolean.opBoolean","COPY",EDGE,{"disambiguationData":[TD([makeQuery(id+"F2.opExtrude","SWEPT_FACE",FACE,{"disambiguationData":[OSD([subQ1])]})])],"derivedFrom":makeQuery(id+"F28.opExtrude","SWEPT_EDGE",EDGE,{"disambiguationData":[OSD([subQ2,sQuery(id+"F19.wireOp",EDGE,"E26.MirrorCS")])]})});}
            var Q4;
            {var subQ1=sQuery(id+"F0.wireOp",EDGE,"E0.right");var subQ2=sQuery(id+"F19.wireOp",EDGE,"E25.MirrorCS");Q4=makeQuery(id+"F28.boolean.opBoolean","COPY",EDGE,{"disambiguationData":[TD([makeQuery(id+"F2.opExtrude","SWEPT_FACE",FACE,{"disambiguationData":[OSD([subQ1])]})])],"derivedFrom":makeQuery(id+"F28.opExtrude","SWEPT_EDGE",EDGE,{"disambiguationData":[OSD([subQ2,sQuery(id+"F19.wireOp",EDGE,"E26.MirrorCS")])]})});}
            var Q5;
            {var subQ1=sQuery(id+"F0.wireOp",EDGE,"E0.right");var subQ2=sQuery(id+"F19.wireOp",EDGE,"E24.MirrorCS");Q5=makeQuery(id+"F28.boolean.opBoolean","COPY",EDGE,{"disambiguationData":[TD([makeQuery(id+"F2.opExtrude","SWEPT_FACE",FACE,{"disambiguationData":[OSD([subQ1])]})])],"derivedFrom":makeQuery(id+"F28.opExtrude","SWEPT_EDGE",EDGE,{"disambiguationData":[OSD([subQ2,sQuery(id+"F19.wireOp",EDGE,"E26.MirrorCS")])]})});}
            var Q6;
            {var subQ1=sQuery(id+"F0.wireOp",EDGE,"E0.right");var subQ2=sQuery(id+"F19.wireOp",EDGE,"E23.right");Q6=makeQuery(id+"F28.boolean.opBoolean","COPY",EDGE,{"disambiguationData":[TD([makeQuery(id+"F2.opExtrude","SWEPT_FACE",FACE,{"disambiguationData":[OSD([subQ1])]})])],"derivedFrom":makeQuery(id+"F28.opExtrude","SWEPT_EDGE",EDGE,{"disambiguationData":[OSD([sQuery(id+"F19.wireOp",EDGE,"E23.bottom"),subQ2])]})});}
            var Q7;
            {var subQ1=sQuery(id+"F0.wireOp",EDGE,"E0.right");var subQ2=sQuery(id+"F19.wireOp",EDGE,"E23.left");Q7=makeQuery(id+"F28.boolean.opBoolean","COPY",EDGE,{"disambiguationData":[TD([makeQuery(id+"F2.opExtrude","SWEPT_FACE",FACE,{"disambiguationData":[OSD([subQ1])]})])],"derivedFrom":makeQuery(id+"F28.opExtrude","SWEPT_EDGE",EDGE,{"disambiguationData":[OSD([sQuery(id+"F19.wireOp",EDGE,"E23.bottom"),subQ2])]})});}
            fillet(context, id + "F29", {"entities" : qUnion([Q0, Q1, Q2, Q3, Q4, Q5, Q6, Q7]), "radius" : 5 * mm, "tangentPropagation" : true, "allowEdgeOverflow" : false});
        }
        {
            var Q0;
            Q0=makeQuery(id+"F2.opExtrude","CAP_EDGE",EDGE,{"disambiguationData":[OSD([sQuery(id+"F0.wireOp",EDGE,"E5.7")])],"isStart":false});
            chamfer(context, id + "F30", {"entities" : qUnion([Q0]), "width" : 0.6 * mm, "tangentPropagation" : true});
        }
        {
            var Q0;
            {var subQ0=sQuery(id+"F0.wireOp",EDGE,"E5.2");Q0=makeQuery(id+"F28.boolean.opBoolean","SPLIT",EDGE,{"disambiguationData":[TD([makeQuery(id+"F28.opExtrude","SWEPT_FACE",FACE,{"disambiguationData":[OSD([sQuery(id+"F19.wireOp",EDGE,"E23.right")])]})])],"derivedFrom":makeQuery(id+"F2.opExtrude","CAP_EDGE",EDGE,{"disambiguationData":[OSD([subQ0])],"isStart":false})});}
            var Q1;
            {var subQ0=sQuery(id+"F0.wireOp",EDGE,"E5.4");var subQ1=sQuery(id+"F0.wireOp",EDGE,"E5.2");Q1=makeQuery(id+"F28.boolean.opBoolean","SPLIT",EDGE,{"disambiguationData":[TD([makeQuery(id+"F2.opExtrude","SWEPT_FACE",FACE,{"disambiguationData":[OSD([subQ0])]})])],"derivedFrom":makeQuery(id+"F2.opExtrude","CAP_EDGE",EDGE,{"disambiguationData":[OSD([subQ1])],"isStart":false})});}
            var Q2;
            {var subQ0=sQuery(id+"F0.wireOp",EDGE,"E5.2");var subQ1=sQuery(id+"F0.wireOp",EDGE,"E5.0");Q2=makeQuery(id+"F28.boolean.opBoolean","SPLIT",EDGE,{"disambiguationData":[TD([makeQuery(id+"F2.opExtrude","SWEPT_FACE",FACE,{"disambiguationData":[OSD([subQ1])]})])],"derivedFrom":makeQuery(id+"F2.opExtrude","CAP_EDGE",EDGE,{"disambiguationData":[OSD([subQ0])],"isStart":false})});}
            chamfer(context, id + "F31", {"entities" : qUnion([Q0, Q1, Q2]), "width" : 0.6 * mm, "tangentPropagation" : true});
        }
        {
            var Q0;
            {var subQ1=sQuery(id+"F0.wireOp",EDGE,"E6.6");var subQ8=sQuery(id+"F0.wireOp",EDGE,"E6.7");var subQ9=sQuery(id+"F0.wireOp",EDGE,"E6.3");var subQ12=sQuery(id+"F0.wireOp",EDGE,"E6.4");var subQ14=sQuery(id+"F0.wireOp",EDGE,"E6.5");var subQ15=sQuery(id+"F0.wireOp",EDGE,"E6.2");var subQ16=sQuery(id+"F0.wireOp",EDGE,"E6.1");var subQ17=sQuery(id+"F0.wireOp",EDGE,"E6.0");var subQ18=sQuery(id+"F0.wireOp",EDGE,"E4.filletArc");var subQ19=sQuery(id+"F0.wireOp",EDGE,"E3.filletArc");var subQ20=sQuery(id+"F0.wireOp",EDGE,"E2.filletArc");var subQ21=sQuery(id+"F0.wireOp",EDGE,"E1.filletArc");var subQ22=sQuery(id+"F0.wireOp",EDGE,"E0.top");var subQ23=sQuery(id+"F0.wireOp",EDGE,"E0.bottom");var subQ24=makeQuery(id+"F3.opExtrude","CAP_FACE",FACE,{"disambiguationData":[OSD([subQ23,subQ22,sQuery(id+"F0.wireOp",EDGE,"E0.left"),sQuery(id+"F0.wireOp",EDGE,"E0.right"),subQ21,subQ20,subQ19,subQ18,subQ17,subQ16,subQ15,subQ9,subQ12,subQ14,subQ1,subQ8])],"isStart":false});var subQ38=subQ24;Q0=makeQuery(id+"F31.opChamfer","MERGE",FACE,{"derivedFrom":[makeQuery(id+"F15.boolean.opBoolean","SPLIT",FACE,{"disambiguationData":[TD([makeQuery(id+"F1.opExtrude","SWEPT_FACE",FACE,{"disambiguationData":[OSD([subQ17])]})])],"derivedFrom":subQ38}),makeQuery(id+"F15.boolean.opBoolean","SPLIT",FACE,{"disambiguationData":[TD([makeQuery(id+"F1.opExtrude","SWEPT_FACE",FACE,{"disambiguationData":[OSD([subQ14])]})])],"derivedFrom":subQ38})]});}
            var sketch = newSketch(context, id + "F32", { "sketchPlane" : qUnion([Q0])});
            skArc(sketch, "E35.0", {"start": v(0, -19.3) * mm, "mid": v(4.16, -19.7) * mm, "end": v(8.17, -20.91) * mm});
            skArc(sketch, "E35.1", {"start": v(-8.17, -20.91) * mm, "mid": v(-4.16, -19.7) * mm, "end": v(0, -19.3) * mm});
            skLineSegment(sketch, "E36", {"start": v(-8.17, -20.91) * mm, "end": v(-7.6, -22.3) * mm});
            skLineSegment(sketch, "E37", {"start": v(8.17, -20.91) * mm, "end": v(7.6, -22.3) * mm});
            skArc(sketch, "E38.0", {"start": v(0, 19.3) * mm, "mid": v(4.16, 19.7) * mm, "end": v(8.17, 20.91) * mm});
            skArc(sketch, "E38.1", {"start": v(-8.17, 20.91) * mm, "mid": v(-4.16, 19.7) * mm, "end": v(0, 19.3) * mm});
            skLineSegment(sketch, "E39", {"start": v(8.17, 20.91) * mm, "end": v(7.6, 22.3) * mm});
            skLineSegment(sketch, "E40", {"start": v(-8.17, 20.91) * mm, "end": v(-7.6, 22.3) * mm});
            skLineSegment(sketch, "E41", {"start": v(-7.6, -22.3) * mm, "end": v(7.6, -22.3) * mm});
            skLineSegment(sketch, "E42", {"start": v(-7.6, 22.3) * mm, "end": v(7.6, 22.3) * mm});
            skSolve(sketch);
        }
        {
            var Q0;
            {var subQ42=sQuery(id+"F32.wireOp",EDGE,"E38.1");var subQ43=sQuery(id+"F32.wireOp",EDGE,"E38.0");var subQ44=makeQuery(id+"F32.imprint","INTERSECT",VERTEX,{"derivedFrom":[subQ43,subQ42]});Q0=makeQuery(id+"F32.imprint","IMPRINT",FACE,{"disambiguationData":[TD([[makeQuery(id+"F32.imprint","IMPRINT",EDGE,{"disambiguationData":[TD([[subQ44,-1.0]])],"derivedFrom":subQ43}),1.0]])]});}
            var Q1;
            {var subQ43=sQuery(id+"F32.wireOp",EDGE,"E35.1");var subQ44=sQuery(id+"F32.wireOp",EDGE,"E35.0");var subQ45=makeQuery(id+"F32.imprint","INTERSECT",VERTEX,{"derivedFrom":[subQ44,subQ43]});Q1=makeQuery(id+"F32.imprint","IMPRINT",FACE,{"disambiguationData":[TD([[makeQuery(id+"F32.imprint","IMPRINT",EDGE,{"disambiguationData":[TD([[subQ45,-1.0]])],"derivedFrom":subQ44}),-1.0]])]});}
            extrude(context, id + "F33", {"entities" : qUnion([Q0, Q1]), "operationType" : NewBodyOperationType.REMOVE, "endBound" : BoundingType.THROUGH_ALL, "depth" : 25 * mm, "offsetDistance" : 25 * mm});
        }
        {
            var Q0;
            Q0=makeQuery(id+"F2.opExtrude","CAP_EDGE",EDGE,{"disambiguationData":[OSD([sQuery(id+"F0.wireOp",EDGE,"E7.right")])],"isStart":false});
            var Q1;
            Q1=makeQuery(id+"F2.opExtrude","CAP_EDGE",EDGE,{"disambiguationData":[OSD([sQuery(id+"F0.wireOp",EDGE,"E8.MirrorCS")])],"isStart":false});
            var Q2;
            Q2=makeQuery(id+"F2.opExtrude","CAP_EDGE",EDGE,{"disambiguationData":[OSD([sQuery(id+"F0.wireOp",EDGE,"E12.MirrorCS")])],"isStart":false});
            var Q3;
            Q3=makeQuery(id+"F2.opExtrude","CAP_EDGE",EDGE,{"disambiguationData":[OSD([sQuery(id+"F0.wireOp",EDGE,"E15.MirrorCS")])],"isStart":false});
            chamfer(context, id + "F34", {"entities" : qUnion([Q0, Q1, Q2, Q3]), "width" : 1 * mm});
        }
    });
